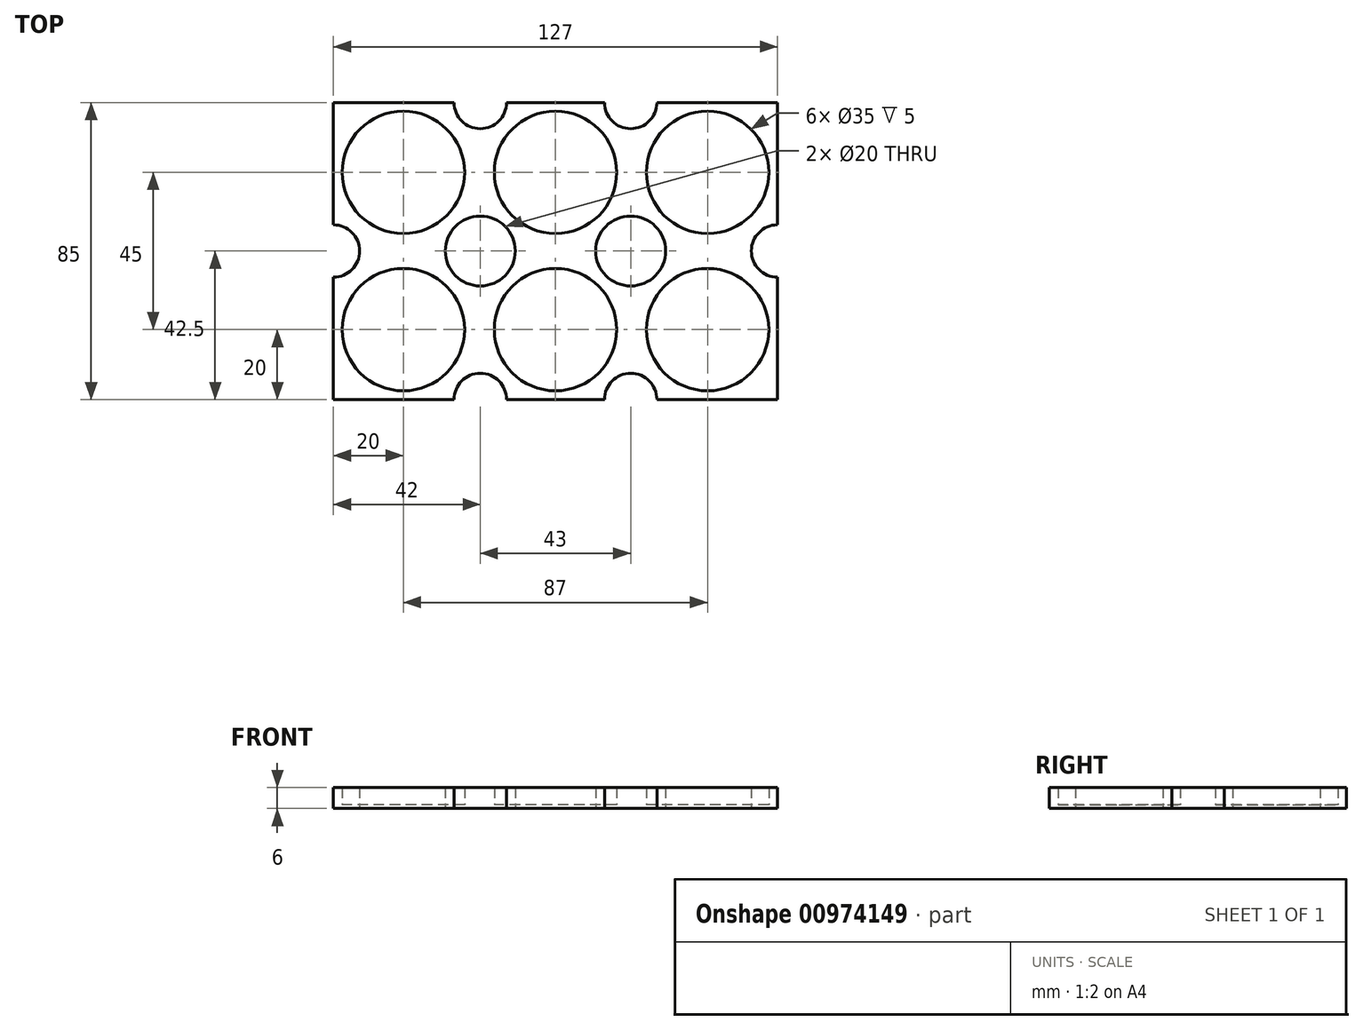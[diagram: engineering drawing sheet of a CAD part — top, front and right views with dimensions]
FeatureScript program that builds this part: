
annotation { "Feature Type Name" : "Feature", "Feature Type Description" : "" }
export const myFeature = defineFeature(function(context is Context, id is Id, definition is map)
    precondition{}
    {
        {
            var Q0;
            Q0=qCreatedBy(makeId("Top.planeOp"),FACE);
            var sketch = newSketch(context, id + "F0", { "sketchPlane" : qUnion([Q0])});
            skLineSegment(sketch, "E0.bottom", {"start": v(-63.5, 42.5) * mm, "end": v(63.5, 42.5) * mm});
            skLineSegment(sketch, "E0.top", {"start": v(-63.5, -42.5) * mm, "end": v(63.5, -42.5) * mm});
            skLineSegment(sketch, "E0.left", {"start": v(-63.5, 42.5) * mm, "end": v(-63.5, -42.5) * mm});
            skLineSegment(sketch, "E0.right", {"start": v(63.5, 42.5) * mm, "end": v(63.5, -42.5) * mm});
            skPoint(sketch, "E0.middle", {"position": v(0, 0) * mm});
            skCircle(sketch, "E1", {"center": v(0, 22.5) * mm, "radius": 17.5 * mm});
            skCircle(sketch, "E2", {"center": v(0, -22.5) * mm, "radius": 17.5 * mm});
            skCircle(sketch, "E3", {"center": v(-43.5, 22.5) * mm, "radius": 17.5 * mm});
            skCircle(sketch, "E4", {"center": v(-43.5, -22.5) * mm, "radius": 17.5 * mm});
            skCircle(sketch, "E5", {"center": v(43.5, -22.5) * mm, "radius": 17.5 * mm});
            skCircle(sketch, "E6", {"center": v(43.5, 22.5) * mm, "radius": 17.5 * mm});
            skCircle(sketch, "E7", {"center": v(-21.5, 0) * mm, "radius": 10 * mm});
            skCircle(sketch, "E8", {"center": v(21.5, 0) * mm, "radius": 10 * mm});
            skCircle(sketch, "E9", {"center": v(-21.5, 42.5) * mm, "radius": 7.5 * mm});
            skCircle(sketch, "E10", {"center": v(21.5, 42.5) * mm, "radius": 7.5 * mm});
            skCircle(sketch, "E11", {"center": v(21.5, -42.5) * mm, "radius": 7.5 * mm});
            skCircle(sketch, "E12", {"center": v(-21.5, -42.5) * mm, "radius": 7.5 * mm});
            skCircle(sketch, "E13", {"center": v(-63.5, 0) * mm, "radius": 7.5 * mm});
            skCircle(sketch, "E14", {"center": v(63.5, 0) * mm, "radius": 7.5 * mm});
            skSolve(sketch);
        }
        {
            var Q0;
            Q0=makeQuery(id+"F0.imprint","IMPRINT",FACE,{"disambiguationData":[TD([[makeQuery(id+"F0.imprint","IMPRINT",EDGE,{"derivedFrom":sQuery(id+"F0.wireOp",EDGE,"E1")}),-1.0]])]});
            extrude(context, id + "F1", {"entities" : qUnion([Q0]), "depth" : 6 * mm, "offsetDistance" : 25 * mm});
        }
        {
            var Q0;
            Q0=makeQuery(id+"F0.imprint","IMPRINT",FACE,{"disambiguationData":[TD([[makeQuery(id+"F0.imprint","IMPRINT",EDGE,{"derivedFrom":sQuery(id+"F0.wireOp",EDGE,"E3")}),1.0]])]});
            var Q1;
            Q1=makeQuery(id+"F0.imprint","IMPRINT",FACE,{"disambiguationData":[TD([[makeQuery(id+"F0.imprint","IMPRINT",EDGE,{"derivedFrom":sQuery(id+"F0.wireOp",EDGE,"E1")}),1.0]])]});
            var Q2;
            Q2=makeQuery(id+"F0.imprint","IMPRINT",FACE,{"disambiguationData":[TD([[makeQuery(id+"F0.imprint","IMPRINT",EDGE,{"derivedFrom":sQuery(id+"F0.wireOp",EDGE,"E6")}),1.0]])]});
            var Q3;
            Q3=makeQuery(id+"F0.imprint","IMPRINT",FACE,{"disambiguationData":[TD([[makeQuery(id+"F0.imprint","IMPRINT",EDGE,{"derivedFrom":sQuery(id+"F0.wireOp",EDGE,"E5")}),1.0]])]});
            var Q4;
            Q4=makeQuery(id+"F0.imprint","IMPRINT",FACE,{"disambiguationData":[TD([[makeQuery(id+"F0.imprint","IMPRINT",EDGE,{"derivedFrom":sQuery(id+"F0.wireOp",EDGE,"E2")}),1.0]])]});
            var Q5;
            Q5=makeQuery(id+"F0.imprint","IMPRINT",FACE,{"disambiguationData":[TD([[makeQuery(id+"F0.imprint","IMPRINT",EDGE,{"derivedFrom":sQuery(id+"F0.wireOp",EDGE,"E4")}),1.0]])]});
            extrude(context, id + "F2", {"entities" : qUnion([Q0, Q1, Q2, Q3, Q4, Q5]), "operationType" : NewBodyOperationType.ADD, "depth" : 1 * mm, "offsetDistance" : 25 * mm});
        }
    });
